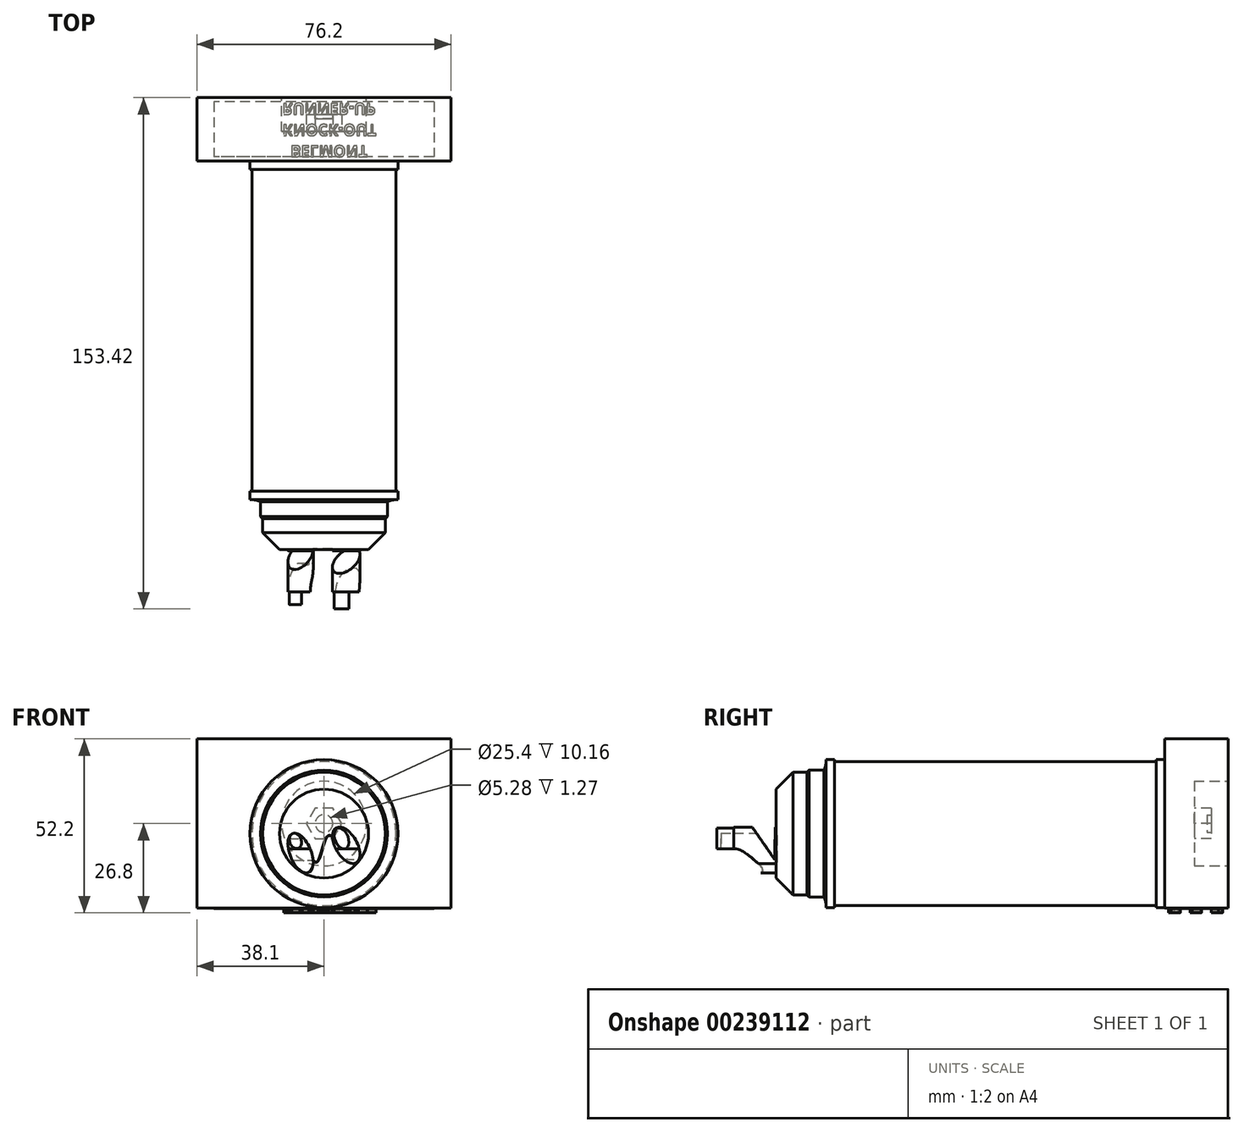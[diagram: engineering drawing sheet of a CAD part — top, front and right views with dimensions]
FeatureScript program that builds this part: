
annotation { "Feature Type Name" : "Feature", "Feature Type Description" : "" }
export const myFeature = defineFeature(function(context is Context, id is Id, definition is map)
    precondition{}
    {
        {
            var Q0;
            Q0=qCreatedBy(makeId("Front.planeOp"),FACE);
            var sketch = newSketch(context, id + "F0", { "sketchPlane" : qUnion([Q0])});
            skLineSegment(sketch, "E0.bottom", {"start": v(38.1, 25.4) * mm, "end": v(-38.1, 25.4) * mm});
            skLineSegment(sketch, "E0.top", {"start": v(38.1, -25.4) * mm, "end": v(-38.1, -25.4) * mm});
            skLineSegment(sketch, "E0.left", {"start": v(38.1, 25.4) * mm, "end": v(38.1, -25.4) * mm});
            skLineSegment(sketch, "E0.right", {"start": v(-38.1, 25.4) * mm, "end": v(-38.1, -25.4) * mm});
            skPoint(sketch, "E0.middle", {"position": v(0, 0) * mm});
            skSolve(sketch);
        }
        {
            var Q0;
            Q0 = qSketchRegion(id + "F0", true);
            extrude(context, id + "F1", {"entities" : qUnion([Q0]), "endBound" : BoundingType.SYMMETRIC, "depth" : 19.05 * mm});
        }
        {
            var Q0;
            Q0=makeQuery(id+"F1.opExtrude","CAP_FACE",FACE,{"disambiguationData":[OSD([sQuery(id+"F0.wireOp",EDGE,"E0.bottom"),sQuery(id+"F0.wireOp",EDGE,"E0.top"),sQuery(id+"F0.wireOp",EDGE,"E0.left"),sQuery(id+"F0.wireOp",EDGE,"E0.right")])],"isStart":false});
            var sketch = newSketch(context, id + "F2", { "sketchPlane" : qUnion([Q0])});
            skCircle(sketch, "E1", {"center": v(0, -3) * mm, "radius": 22.23 * mm});
            skSolve(sketch);
        }
        {
            var Q0;
            Q0 = qSketchRegion(id + "F2", true);
            extrude(context, id + "F3", {"entities" : qUnion([Q0]), "operationType" : NewBodyOperationType.ADD, "endBound" : BoundingType.SYMMETRIC, "depth" : 5.08 * mm});
        }
        {
            var Q0;
            Q0=makeQuery(id+"F3.opExtrude","CAP_FACE",FACE,{"disambiguationData":[OSD([sQuery(id+"F2.wireOp",EDGE,"E1")])],"isStart":false});
            var sketch = newSketch(context, id + "F4", { "sketchPlane" : qUnion([Q0])});
            skCircle(sketch, "E2", {"center": v(0, -3) * mm, "radius": 21.59 * mm});
            skSolve(sketch);
        }
        {
            var Q0;
            Q0 = qSketchRegion(id + "F4", true);
            extrude(context, id + "F5", {"entities" : qUnion([Q0]), "operationType" : NewBodyOperationType.ADD, "depth" : 96.52 * mm});
        }
        {
            var Q0;
            Q0=makeQuery(id+"F5.opExtrude","CAP_FACE",FACE,{"disambiguationData":[OSD([sQuery(id+"F4.wireOp",EDGE,"E2")])],"isStart":false});
            var sketch = newSketch(context, id + "F6", { "sketchPlane" : qUnion([Q0])});
            skCircle(sketch, "E3", {"center": v(0, -3) * mm, "radius": 22.23 * mm});
            skSolve(sketch);
        }
        {
            var Q0;
            Q0 = qSketchRegion(id + "F6", true);
            extrude(context, id + "F7", {"entities" : qUnion([Q0]), "operationType" : NewBodyOperationType.ADD, "depth" : 2.54 * mm});
        }
        {
            var Q0;
            Q0=makeQuery(id+"F7.opExtrude","CAP_FACE",FACE,{"disambiguationData":[OSD([sQuery(id+"F6.wireOp",EDGE,"E3")])],"isStart":false});
            var sketch = newSketch(context, id + "F8", { "sketchPlane" : qUnion([Q0])});
            skCircle(sketch, "E4", {"center": v(0, -3) * mm, "radius": 19.69 * mm});
            skSolve(sketch);
        }
        {
            var Q0;
            Q0 = qSketchRegion(id + "F8", true);
            extrude(context, id + "F9", {"entities" : qUnion([Q0]), "operationType" : NewBodyOperationType.ADD, "depth" : 5.08 * mm});
        }
        {
            var Q0;
            Q0=makeQuery(id+"F9.opExtrude","CAP_FACE",FACE,{"disambiguationData":[OSD([sQuery(id+"F8.wireOp",EDGE,"E4")])],"isStart":false});
            var sketch = newSketch(context, id + "F10", { "sketchPlane" : qUnion([Q0])});
            skCircle(sketch, "E5", {"center": v(0, -3) * mm, "radius": 19.05 * mm});
            skSolve(sketch);
        }
        {
            var Q0;
            Q0 = qSketchRegion(id + "F10", true);
            extrude(context, id + "F11", {"entities" : qUnion([Q0]), "operationType" : NewBodyOperationType.ADD, "depth" : 5.08 * mm});
        }
        {
            var Q0;
            Q0=makeQuery(id+"F11.opExtrude","CAP_FACE",FACE,{"disambiguationData":[OSD([sQuery(id+"F10.wireOp",EDGE,"E5")])],"isStart":false});
            var sketch = newSketch(context, id + "F12", { "sketchPlane" : qUnion([Q0])});
            skCircle(sketch, "E6", {"center": v(0, -3) * mm, "radius": 18.41 * mm});
            skSolve(sketch);
        }
        {
            var Q0;
            Q0 = qSketchRegion(id + "F12", true);
            extrude(context, id + "F13", {"entities" : qUnion([Q0]), "operationType" : NewBodyOperationType.ADD, "depth" : 4.83 * mm});
        }
        {
            var Q0;
            Q0=makeQuery(id+"F9.opExtrude","CAP_EDGE",EDGE,{"disambiguationData":[OSD([sQuery(id+"F8.wireOp",EDGE,"E4")])],"isStart":false});
            chamfer(context, id + "F14", {"entities" : qUnion([Q0]), "width" : 5.08 * mm, "tangentPropagation" : true});
        }
        {
            var Q0;
            Q0=makeQuery(id+"F11.opExtrude","CAP_EDGE",EDGE,{"disambiguationData":[OSD([sQuery(id+"F10.wireOp",EDGE,"E5")])],"isStart":false});
            chamfer(context, id + "F15", {"entities" : qUnion([Q0]), "width" : 5.08 * mm, "tangentPropagation" : true});
        }
        {
            var Q0;
            Q0=makeQuery(id+"F13.opExtrude","CAP_EDGE",EDGE,{"disambiguationData":[OSD([sQuery(id+"F12.wireOp",EDGE,"E6")])],"isStart":false});
            chamfer(context, id + "F16", {"entities" : qUnion([Q0]), "width" : 5.08 * mm, "tangentPropagation" : true});
        }
        {
            var Q0;
            Q0=makeQuery(id+"F1.opExtrude","CAP_FACE",FACE,{"disambiguationData":[OSD([sQuery(id+"F0.wireOp",EDGE,"E0.bottom"),sQuery(id+"F0.wireOp",EDGE,"E0.top"),sQuery(id+"F0.wireOp",EDGE,"E0.left"),sQuery(id+"F0.wireOp",EDGE,"E0.right")])],"isStart":true});
            var sketch = newSketch(context, id + "F17", { "sketchPlane" : qUnion([Q0])});
            skCircle(sketch, "E7", {"center": v(0, 0) * mm, "radius": 12.7 * mm});
            skSolve(sketch);
        }
        {
            var Q0;
            Q0 = qSketchRegion(id + "F17", true);
            extrude(context, id + "F18", {"entities" : qUnion([Q0]), "operationType" : NewBodyOperationType.REMOVE, "oppositeDirection" : true, "depth" : 10.16 * mm});
        }
        {
            var Q0;
            Q0=makeQuery(id+"F18.boolean.opBoolean","COPY",FACE,{"derivedFrom":makeQuery(id+"F18.opExtrude","CAP_FACE",FACE,{"disambiguationData":[OSD([sQuery(id+"F17.wireOp",EDGE,"E7")])],"isStart":false})});
            var sketch = newSketch(context, id + "F19", { "sketchPlane" : qUnion([Q0])});
            skCircle(sketch, "E8.cCircle", {"center": v(0, 0) * mm, "radius": 5.28 * mm, "construction": true});
            skLineSegment(sketch, "E8.0", {"start": v(5.28, 0) * mm, "end": v(2.64, -4.57) * mm});
            skLineSegment(sketch, "E8.1", {"start": v(2.64, -4.57) * mm, "end": v(-2.64, -4.57) * mm});
            skLineSegment(sketch, "E8.2", {"start": v(-2.64, -4.57) * mm, "end": v(-5.28, 0) * mm});
            skLineSegment(sketch, "E8.3", {"start": v(-5.28, 0) * mm, "end": v(-2.64, 4.57) * mm});
            skLineSegment(sketch, "E8.4", {"start": v(-2.64, 4.57) * mm, "end": v(2.64, 4.57) * mm});
            skLineSegment(sketch, "E8.5", {"start": v(2.64, 4.57) * mm, "end": v(5.28, 0) * mm});
            skSolve(sketch);
        }
        {
            var Q0;
            Q0 = qSketchRegion(id + "F19", true);
            extrude(context, id + "F20", {"entities" : qUnion([Q0]), "operationType" : NewBodyOperationType.ADD, "depth" : 5.08 * mm});
        }
        {
            var Q0;
            Q0=makeQuery(id+"F20.opExtrude","CAP_FACE",FACE,{"disambiguationData":[OSD([sQuery(id+"F19.wireOp",EDGE,"E8.0"),sQuery(id+"F19.wireOp",EDGE,"E8.1"),sQuery(id+"F19.wireOp",EDGE,"E8.2"),sQuery(id+"F19.wireOp",EDGE,"E8.3"),sQuery(id+"F19.wireOp",EDGE,"E8.4"),sQuery(id+"F19.wireOp",EDGE,"E8.5")])],"isStart":false});
            var sketch = newSketch(context, id + "F21", { "sketchPlane" : qUnion([Q0])});
            skCircle(sketch, "E9", {"center": v(0, 0) * mm, "radius": 2.64 * mm});
            skSolve(sketch);
        }
        {
            var Q0;
            Q0 = qSketchRegion(id + "F21", true);
            extrude(context, id + "F22", {"entities" : qUnion([Q0]), "operationType" : NewBodyOperationType.REMOVE, "oppositeDirection" : true, "depth" : 1.27 * mm});
        }
        {
            var Q0;
            Q0=makeQuery(id+"F1.opExtrude","SWEPT_FACE",FACE,{"disambiguationData":[OSD([sQuery(id+"F0.wireOp",EDGE,"E0.top")])]});
            var sketch = newSketch(context, id + "F23", { "sketchPlane" : qUnion([Q0])});
            skLineSegment(sketch, "E10.bottom", {"start": v(33.02, -8.26) * mm, "end": v(-33.02, -8.26) * mm});
            skLineSegment(sketch, "E10.top", {"start": v(33.02, 8.26) * mm, "end": v(-33.02, 8.26) * mm});
            skLineSegment(sketch, "E10.left", {"start": v(33.02, -8.26) * mm, "end": v(33.02, 8.25) * mm});
            skLineSegment(sketch, "E10.right", {"start": v(-33.02, -8.26) * mm, "end": v(-33.02, 8.25) * mm});
            skPoint(sketch, "E10.middle", {"position": v(0, 0) * mm});
            skSolve(sketch);
        }
        {
            var Q0;
            Q0 = qSketchRegion(id + "F23", true);
            extrude(context, id + "F24", {"entities" : qUnion([Q0]), "operationType" : NewBodyOperationType.ADD, "depth" : 0.13 * mm});
        }
        {
            var Q0;
            Q0=makeQuery(id+"F13.opExtrude","CAP_FACE",FACE,{"disambiguationData":[OSD([sQuery(id+"F12.wireOp",EDGE,"E6")])],"isStart":false});
            var sketch = newSketch(context, id + "F25", { "sketchPlane" : qUnion([Q0])});
            skEllipse(sketch, "E11", {"center": v(-7.03, -8.87) * mm, "majorRadius": 6.35 * mm, "minorRadius": 3.18 * mm, "majorAxis": v(-0.38, 0.93)});
            skSolve(sketch);
        }
        {
            var Q0;
            Q0 = qSketchRegion(id + "F25", true);
            extrude(context, id + "F26", {"entities" : qUnion([Q0]), "operationType" : NewBodyOperationType.ADD, "depth" : 12.7 * mm});
        }
        {
            var Q0;
            Q0=makeQuery(id+"F26.opExtrude","CAP_FACE",FACE,{"disambiguationData":[OSD([sQuery(id+"F25.wireOp",EDGE,"E11")])],"isStart":false});
            var sketch = newSketch(context, id + "F27", { "sketchPlane" : qUnion([Q0])});
            skEllipse(sketch, "E12", {"center": v(-8.56, -5.23) * mm, "majorRadius": 2.37 * mm, "minorRadius": 1.75 * mm, "majorAxis": v(-0.36, 0.93)});
            skSolve(sketch);
        }
        {
            var Q0;
            Q0 = qSketchRegion(id + "F27", true);
            extrude(context, id + "F28", {"entities" : qUnion([Q0]), "operationType" : NewBodyOperationType.ADD, "depth" : 3.8 * mm});
        }
        {
            var Q0;
            Q0=qCreatedBy(makeId("Right.planeOp"),FACE);
            var sketch = newSketch(context, id + "F29", { "sketchPlane" : qUnion([Q0])});
            skLineSegment(sketch, "E13", {"start": v(-126.4, -2.69) * mm, "end": v(-132.22, -2.69) * mm});
            skLineSegment(sketch, "E14", {"start": v(-132.22, -2.69) * mm, "end": v(-126.4, -11) * mm});
            skLineSegment(sketch, "E15", {"start": v(-126.4, -11) * mm, "end": v(-126.4, -2.69) * mm});
            skSolve(sketch);
        }
        {
            var Q0;
            Q0 = qSketchRegion(id + "F29", true);
            extrude(context, id + "F30", {"entities" : qUnion([Q0]), "operationType" : NewBodyOperationType.REMOVE, "endBound" : BoundingType.SYMMETRIC, "oppositeDirection" : true, "depth" : 76.2 * mm});
        }
        {
            var Q0;
            Q0=makeQuery(id+"F13.opExtrude","CAP_FACE",FACE,{"disambiguationData":[OSD([sQuery(id+"F12.wireOp",EDGE,"E6")])],"isStart":false});
            var sketch = newSketch(context, id + "F31", { "sketchPlane" : qUnion([Q0])});
            skEllipse(sketch, "E16", {"center": v(6.66, -6.52) * mm, "majorRadius": 6.02 * mm, "minorRadius": 3.25 * mm, "majorAxis": v(-0.5, 0.86)});
            skSolve(sketch);
        }
        {
            var Q0;
            Q0 = qSketchRegion(id + "F31", true);
            extrude(context, id + "F32", {"entities" : qUnion([Q0]), "operationType" : NewBodyOperationType.ADD, "depth" : 12.7 * mm});
        }
        {
            var Q0;
            Q0=qCreatedBy(makeId("Right.planeOp"),FACE);
            var sketch = newSketch(context, id + "F33", { "sketchPlane" : qUnion([Q0])});
            skFitSpline(sketch, "E17", {"points": [v(-139.2, -7.55) * mm, v(-136.89, -7.93) * mm, v(-134.39, -9.47) * mm, v(-131.8, -11.68) * mm, v(-130.35, -14.57) * mm, v(-145.54, -15.62) * mm, v(-143.33, -9.28) * mm, v(-139.2, -7.55) * mm]});
            skSolve(sketch);
        }
        {
            var Q0;
            Q0 = qSketchRegion(id + "F33", true);
            extrude(context, id + "F34", {"entities" : qUnion([Q0]), "operationType" : NewBodyOperationType.REMOVE, "endBound" : BoundingType.SYMMETRIC, "oppositeDirection" : true, "depth" : 76.2 * mm});
        }
        {
            var Q0;
            Q0=qCreatedBy(makeId("Right.planeOp"),FACE);
            var sketch = newSketch(context, id + "F35", { "sketchPlane" : qUnion([Q0])});
            skLineSegment(sketch, "E18", {"start": v(-126.5, -10.79) * mm, "end": v(-133.45, -0.76) * mm});
            skLineSegment(sketch, "E19", {"start": v(-133.45, -0.76) * mm, "end": v(-126.34, -0.76) * mm});
            skLineSegment(sketch, "E20", {"start": v(-126.34, -0.76) * mm, "end": v(-126.5, -10.79) * mm});
            skSolve(sketch);
        }
        {
            var Q0;
            Q0 = qSketchRegion(id + "F35", true);
            extrude(context, id + "F36", {"entities" : qUnion([Q0]), "operationType" : NewBodyOperationType.REMOVE, "endBound" : BoundingType.SYMMETRIC, "oppositeDirection" : true, "depth" : 76.2 * mm});
        }
        {
            var Q0;
            Q0=makeQuery(id+"F32.opExtrude","CAP_FACE",FACE,{"disambiguationData":[OSD([sQuery(id+"F31.wireOp",EDGE,"E16")])],"isStart":false});
            var sketch = newSketch(context, id + "F37", { "sketchPlane" : qUnion([Q0])});
            skSolve(sketch);
        }
        {
            var Q0;
            {var subQ0=sQuery(id+"F31.wireOp",EDGE,"E16");Q0=makeQuery(id+"F37.imprint","IMPRINT",FACE,{"disambiguationData":[TD([[makeQuery(id+"F37.imprint","IMPRINT",EDGE,{"derivedFrom":makeQuery(id+"F32.opExtrude","CAP_EDGE",EDGE,{"disambiguationData":[OSD([subQ0])],"isStart":false})}),1.0]])]});}
            var sketch = newSketch(context, id + "F38", { "sketchPlane" : qUnion([Q0])});
            skEllipse(sketch, "E21", {"center": v(5.26, -4.46) * mm, "majorRadius": 3.3 * mm, "minorRadius": 1.98 * mm, "majorAxis": v(-0.37, 0.93)});
            skSolve(sketch);
        }
        {
            var Q0;
            Q0 = qSketchRegion(id + "F38", true);
            extrude(context, id + "F39", {"entities" : qUnion([Q0]), "operationType" : NewBodyOperationType.ADD, "depth" : 5.08 * mm});
        }
        {
            var Q0;
            Q0=makeQuery(id+"F14.opChamfer","BLEND_EDGE",EDGE,{"blendedFrom":[makeQuery(id+"F9.opExtrude","CAP_EDGE",EDGE,{"disambiguationData":[OSD([sQuery(id+"F8.wireOp",EDGE,"E4")])],"isStart":false}),makeQuery(id+"F7.opExtrude","CAP_FACE",FACE,{"disambiguationData":[OSD([sQuery(id+"F6.wireOp",EDGE,"E3")])],"isStart":false})],"blendedInto":[makeQuery(id+"F7.opExtrude","CAP_FACE",FACE,{"disambiguationData":[OSD([sQuery(id+"F6.wireOp",EDGE,"E3")])],"isStart":false})]});
            fillet(context, id + "F40", {"entities" : qUnion([Q0]), "radius" : 5.08 * mm, "tangentPropagation" : true, "allowEdgeOverflow" : false});
        }
        {
            var Q0;
            Q0=makeQuery(id+"F24.opExtrude","CAP_FACE",FACE,{"disambiguationData":[OSD([sQuery(id+"F23.wireOp",EDGE,"E10.bottom"),sQuery(id+"F23.wireOp",EDGE,"E10.top"),sQuery(id+"F23.wireOp",EDGE,"E10.left"),sQuery(id+"F23.wireOp",EDGE,"E10.right")])],"isStart":false});
            var sketch = newSketch(context, id + "F41", { "sketchPlane" : qUnion([Q0])});
            skText(sketch, "E22", { "text": "  BELMONT\nKNOCK-OUT\nRUNNER-UP", "fontName": "OpenSans-Bold.ttf"});
            const initialGuessF41  = {"E22": [-0.01246, 0.00489, 1, 0, 0.00337]};
            skSetInitialGuess(sketch, initialGuessF41);
            skSolve(sketch);
        }
        {
            var Q0;
            Q0 = qSketchRegion(id + "F41", true);
            extrude(context, id + "F42", {"entities" : qUnion([Q0]), "operationType" : NewBodyOperationType.ADD, "depth" : 1.27 * mm});
        }
        {
            var Q0;
            Q0=makeQuery(id+"F13.opExtrude","CAP_FACE",FACE,{"disambiguationData":[OSD([sQuery(id+"F12.wireOp",EDGE,"E6")])],"isStart":false});
            var sketch = newSketch(context, id + "F43", { "sketchPlane" : qUnion([Q0])});
            skFitSpline(sketch, "E23", {"points": [v(-3.26, -10.96) * mm, v(-2.74, -11.48) * mm, v(-1.81, -11.13) * mm, v(0.51, -4.46) * mm, v(1.7, -3.52) * mm, v(2.53, -3.96) * mm, v(2.53, -4.03) * mm, v(2.17, -3.77) * mm, v(1.46, -3.63) * mm, v(1.2, -3.73) * mm, v(0.87, -4.02) * mm, v(0.16, -5.7) * mm, v(-0.91, -9.28) * mm, v(-1.67, -11.13) * mm, v(-1.8, -11.28) * mm, v(-2.13, -11.57) * mm, v(-2.55, -11.61) * mm, v(-2.99, -11.4) * mm, v(-3.26, -10.96) * mm]});
            skSolve(sketch);
        }
        {
            var Q0;
            Q0 = qSketchRegion(id + "F43", true);
            extrude(context, id + "F44", {"entities" : qUnion([Q0]), "operationType" : NewBodyOperationType.REMOVE, "oppositeDirection" : true, "depth" : 0.25 * mm});
        }
    });
